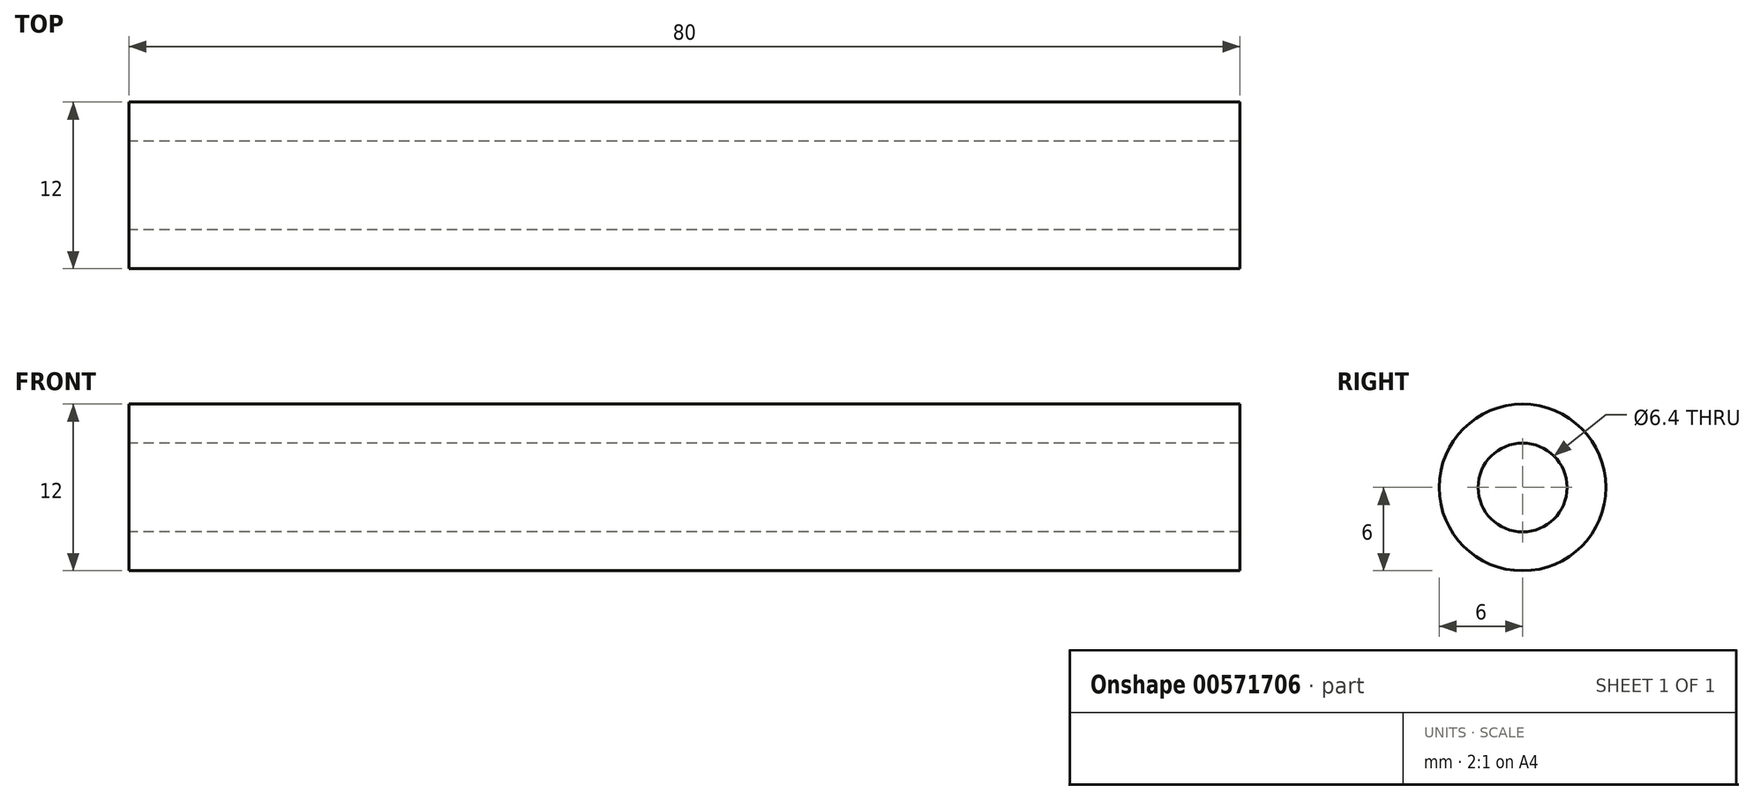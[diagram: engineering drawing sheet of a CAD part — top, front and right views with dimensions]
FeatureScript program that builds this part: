
annotation { "Feature Type Name" : "Feature", "Feature Type Description" : "" }
export const myFeature = defineFeature(function(context is Context, id is Id, definition is map)
    precondition{}
    {
        {
            var Q0;
            Q0=qCreatedBy(makeId("Right.planeOp"),FACE);
            var sketch = newSketch(context, id + "F0", { "sketchPlane" : qUnion([Q0])});
            skCircle(sketch, "E0", {"center": v(0, 0) * mm, "radius": 6 * mm});
            skCircle(sketch, "E1", {"center": v(0, 0) * mm, "radius": 3.2 * mm});
            skSolve(sketch);
        }
        {
            var Q0;
            Q0 = qSketchRegion(id + "F0", true);
            extrude(context, id + "F1", {"entities" : qUnion([Q0]), "endBound" : BoundingType.SYMMETRIC, "depth" : 80 * mm, "offsetDistance" : 25 * mm});
        }
    });
